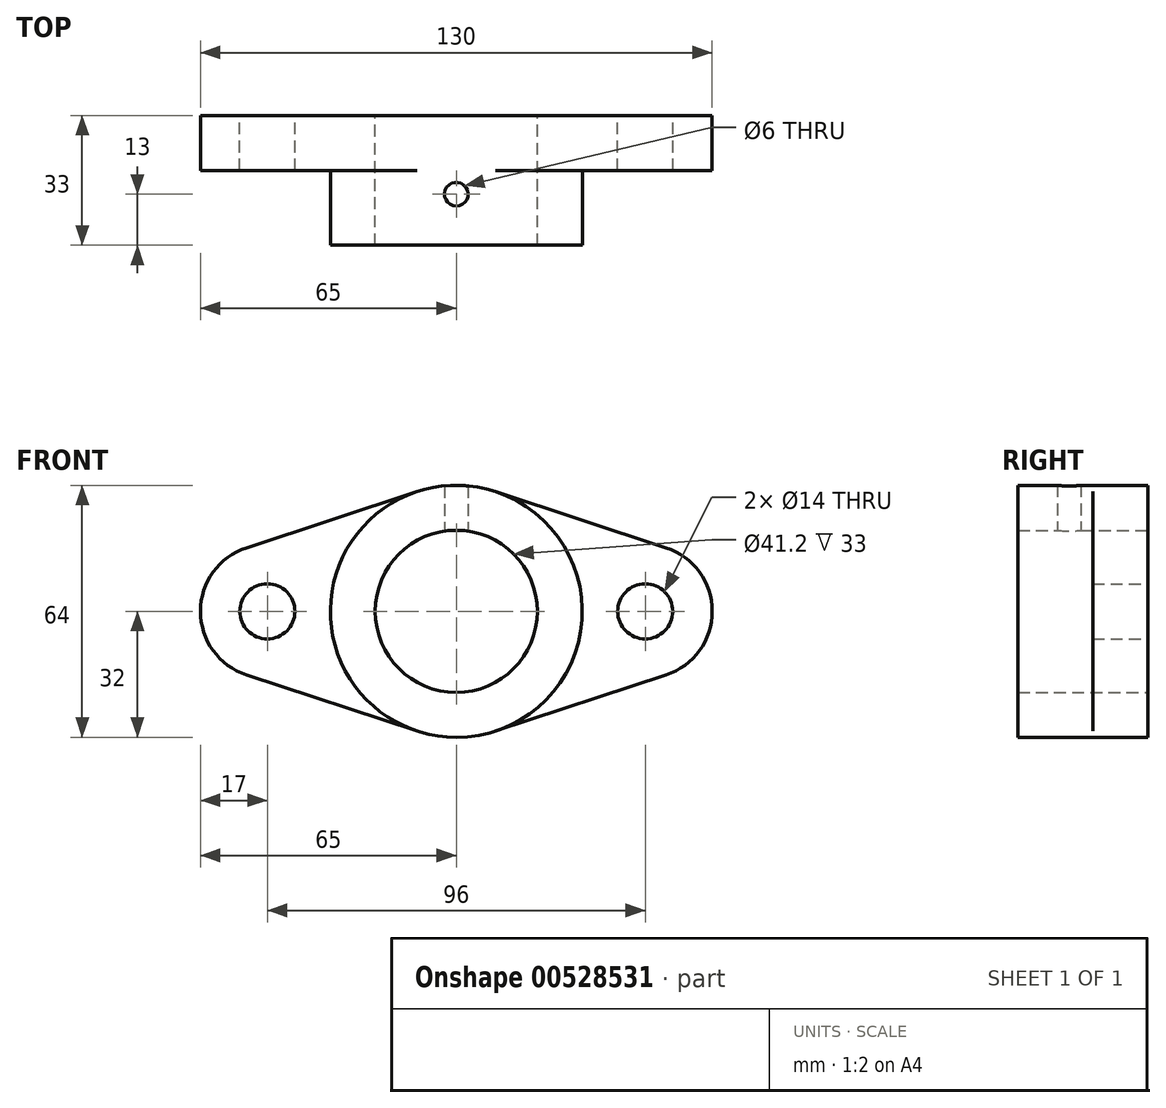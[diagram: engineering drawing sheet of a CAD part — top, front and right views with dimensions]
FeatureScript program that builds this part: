
annotation { "Feature Type Name" : "Feature", "Feature Type Description" : "" }
export const myFeature = defineFeature(function(context is Context, id is Id, definition is map)
    precondition{}
    {
        {
            var Q0;
            Q0=qCreatedBy(makeId("Front.planeOp"),FACE);
            var sketch = newSketch(context, id + "F0", { "sketchPlane" : qUnion([Q0])});
            skArc(sketch, "E0", {"start": v(-10, -30.4) * mm, "mid": v(0, -32) * mm, "end": v(10, -30.4) * mm});
            skArc(sketch, "E1", {"start": v(-53.31, 16.15) * mm, "mid": v(-65, 0) * mm, "end": v(-53.31, -16.15) * mm});
            skCircle(sketch, "E2", {"center": v(-48, 0) * mm, "radius": 7 * mm});
            skLineSegment(sketch, "E3", {"start": v(0, 43.21) * mm, "end": v(0, -56.13) * mm, "construction": true});
            skLineSegment(sketch, "E4", {"start": v(-10, 30.4) * mm, "end": v(-53.31, 16.15) * mm});
            skLineSegment(sketch, "E5", {"start": v(-53.31, -16.15) * mm, "end": v(-10, -30.4) * mm});
            skCircle(sketch, "E6.MirrorC", {"center": v(48, 0) * mm, "radius": 7 * mm});
            skArc(sketch, "E7.MirrorC", {"start": v(53.31, 16.15) * mm, "mid": v(65, 0) * mm, "end": v(53.31, -16.15) * mm});
            skLineSegment(sketch, "E8", {"start": v(10, 30.4) * mm, "end": v(53.31, 16.15) * mm});
            skLineSegment(sketch, "E9", {"start": v(53.31, -16.15) * mm, "end": v(10, -30.4) * mm});
            skArc(sketch, "E10.trimOffspring", {"start": v(10, 30.4) * mm, "mid": v(0, 32) * mm, "end": v(-10, 30.4) * mm});
            skCircle(sketch, "E11", {"center": v(0, 0) * mm, "radius": 20.6 * mm});
            skSolve(sketch);
        }
        {
            var Q0;
            Q0 = qSketchRegion(id + "F0", true);
            extrude(context, id + "F1", {"entities" : qUnion([Q0]), "depth" : 14 * mm, "offsetDistance" : 25 * mm});
        }
        {
            var Q0;
            Q0=makeQuery(id+"F1.opExtrude","CAP_FACE",FACE,{"disambiguationData":[OSD([sQuery(id+"F0.wireOp",EDGE,"E0"),sQuery(id+"F0.wireOp",EDGE,"E1"),sQuery(id+"F0.wireOp",EDGE,"E2"),sQuery(id+"F0.wireOp",EDGE,"E4"),sQuery(id+"F0.wireOp",EDGE,"E5"),sQuery(id+"F0.wireOp",EDGE,"E6.MirrorC"),sQuery(id+"F0.wireOp",EDGE,"E7.MirrorC"),sQuery(id+"F0.wireOp",EDGE,"E8"),sQuery(id+"F0.wireOp",EDGE,"E9"),sQuery(id+"F0.wireOp",EDGE,"E10.trimOffspring"),sQuery(id+"F0.wireOp",EDGE,"E11")])],"isStart":false});
            var sketch = newSketch(context, id + "F2", { "sketchPlane" : qUnion([Q0])});
            skCircle(sketch, "E12.0", {"center": v(0, 0) * mm, "radius": 20.6 * mm});
            skCircle(sketch, "E13", {"center": v(0, 0) * mm, "radius": 32 * mm});
            skSolve(sketch);
        }
        {
            var Q0;
            Q0 = qSketchRegion(id + "F2", true);
            extrude(context, id + "F3", {"entities" : qUnion([Q0]), "operationType" : NewBodyOperationType.ADD, "depth" : (33 - 14) * mm, "offsetDistance" : 25 * mm});
        }
        {
            var Q0;
            Q0=qCreatedBy(makeId("Top.planeOp"),FACE);
            var sketch = newSketch(context, id + "F4", { "sketchPlane" : qUnion([Q0])});
            skCircle(sketch, "E14", {"center": v(0, -20) * mm, "radius": 3 * mm});
            skSolve(sketch);
        }
        {
            var Q0;
            Q0 = qSketchRegion(id + "F4", true);
            extrude(context, id + "F5", {"entities" : qUnion([Q0]), "operationType" : NewBodyOperationType.REMOVE, "endBound" : BoundingType.THROUGH_ALL, "depth" : 25 * mm, "offsetDistance" : 25 * mm});
        }
    });
